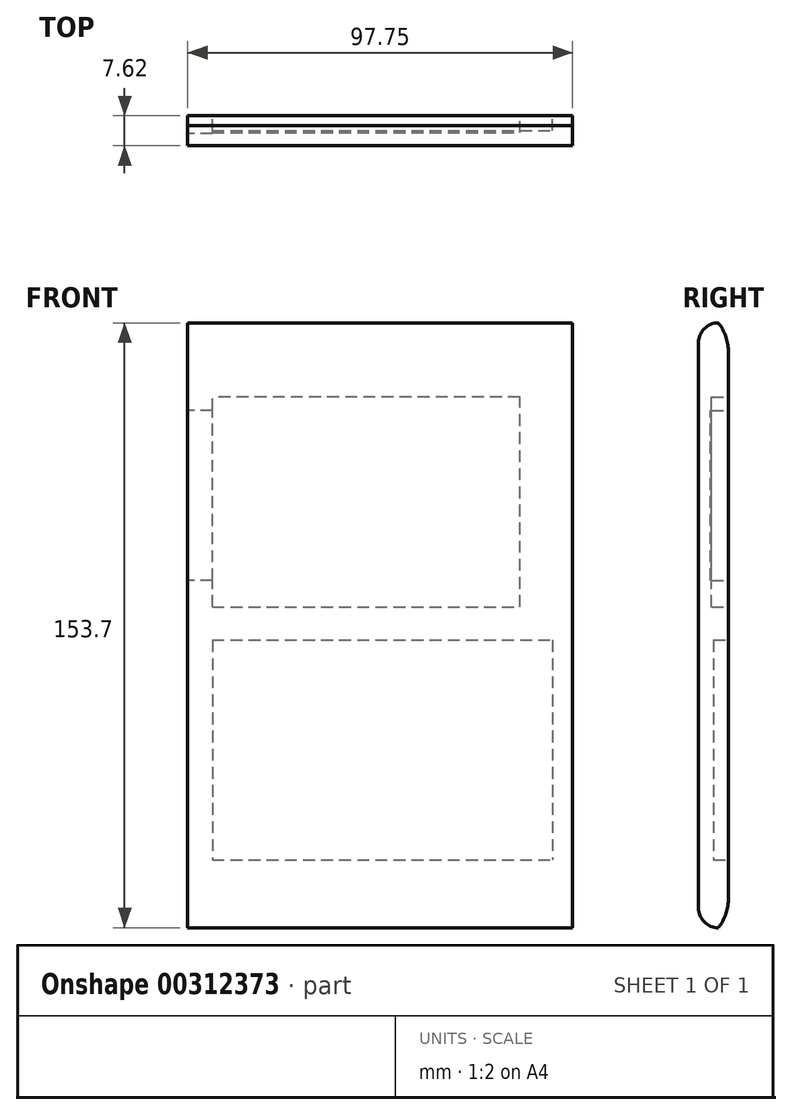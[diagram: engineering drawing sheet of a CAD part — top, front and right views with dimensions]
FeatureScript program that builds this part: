
annotation { "Feature Type Name" : "Feature", "Feature Type Description" : "" }
export const myFeature = defineFeature(function(context is Context, id is Id, definition is map)
    precondition{}
    {
        {
            var Q0;
            Q0=qCreatedBy(makeId("Front.planeOp"),FACE);
            var sketch = newSketch(context, id + "F0", { "sketchPlane" : qUnion([Q0])});
            skLineSegment(sketch, "E0", {"start": v(0, 0) * mm, "end": v(0, 53.34) * mm});
            skLineSegment(sketch, "E1", {"start": v(0, 53.34) * mm, "end": v(64.52, 53.34) * mm});
            skPoint(sketch, "E2", {"position": v(64.52, 53.34) * mm});
            skPoint(sketch, "E3", {"position": v(66.74, 51.82) * mm});
            skPoint(sketch, "E4", {"position": v(66.74, 40.39) * mm});
            skPoint(sketch, "E5", {"position": v(70.53, 37.85) * mm});
            skPoint(sketch, "E6", {"position": v(70.53, 5.08) * mm});
            skPoint(sketch, "E7", {"position": v(66.59, 2.54) * mm});
            skLineSegment(sketch, "E8", {"start": v(0, 0) * mm, "end": v(66.59, 0) * mm});
            skPoint(sketch, "E9.center.orphan", {"position": v(15.24, 50.8) * mm});
            skPoint(sketch, "E10.center.orphan", {"position": v(66.04, 35.56) * mm});
            skPoint(sketch, "E11.center.orphan", {"position": v(66.04, 7.62) * mm});
            skPoint(sketch, "E12.center.orphan", {"position": v(13.97, 2.54) * mm});
            skLineSegment(sketch, "E13", {"start": v(66.59, 0) * mm, "end": v(70.53, 0) * mm});
            skLineSegment(sketch, "E14", {"start": v(64.52, 53.34) * mm, "end": v(70.53, 53.34) * mm});
            skLineSegment(sketch, "E15", {"start": v(70.53, 0) * mm, "end": v(78.15, 0) * mm});
            skLineSegment(sketch, "E16", {"start": v(78.15, 0) * mm, "end": v(78.15, 53.34) * mm});
            skLineSegment(sketch, "E17", {"start": v(78.15, 53.34) * mm, "end": v(70.53, 53.34) * mm});
            skSolve(sketch);
        }
        {
            var Q0;
            Q0=qCreatedBy(makeId("Front.planeOp"),FACE);
            var sketch = newSketch(context, id + "F1", { "sketchPlane" : qUnion([Q0])});
            skLineSegment(sketch, "E18.bottom", {"start": v(0, -8.44) * mm, "end": v(86.36, -8.44) * mm});
            skLineSegment(sketch, "E18.top", {"start": v(0, -64.32) * mm, "end": v(86.36, -64.32) * mm});
            skLineSegment(sketch, "E18.left", {"start": v(0, -8.44) * mm, "end": v(0, -64.32) * mm});
            skLineSegment(sketch, "E18.right", {"start": v(86.36, -8.44) * mm, "end": v(86.36, -64.32) * mm});
            skSolve(sketch);
        }
        {
            var Q0;
            Q0=qCreatedBy(makeId("Front.planeOp"),FACE);
            var sketch = newSketch(context, id + "F2", { "sketchPlane" : qUnion([Q0])});
            skLineSegment(sketch, "E19.left", {"start": v(-6.27, 59.48) * mm, "end": v(-6.27, -68.82) * mm});
            skLineSegment(sketch, "E19.right", {"start": v(91.48, 59.48) * mm, "end": v(91.48, -68.82) * mm});
            skLineSegment(sketch, "E20", {"start": v(-6.27, 59.48) * mm, "end": v(-6.27, 72.18) * mm});
            skLineSegment(sketch, "E21", {"start": v(-6.27, 72.18) * mm, "end": v(91.48, 72.18) * mm});
            skLineSegment(sketch, "E22", {"start": v(91.48, 72.18) * mm, "end": v(91.48, 59.48) * mm});
            skLineSegment(sketch, "E23", {"start": v(-6.27, -68.82) * mm, "end": v(-6.27, -81.52) * mm});
            skLineSegment(sketch, "E24", {"start": v(-6.27, -81.52) * mm, "end": v(91.48, -81.52) * mm});
            skLineSegment(sketch, "E25", {"start": v(91.48, -81.52) * mm, "end": v(91.48, -68.82) * mm});
            skSolve(sketch);
        }
        {
            var Q0;
            Q0 = qSketchRegion(id + "F2", true);
            extrude(context, id + "F3", {"entities" : qUnion([Q0]), "depth" : 7.62 * mm});
        }
        {
            var Q0;
            Q0 = qSketchRegion(id + "F0", true);
            extrude(context, id + "F4", {"entities" : qUnion([Q0]), "operationType" : NewBodyOperationType.REMOVE, "depth" : 4.32 * mm});
        }
        {
            var Q0;
            Q0 = qSketchRegion(id + "F1", true);
            extrude(context, id + "F5", {"entities" : qUnion([Q0]), "operationType" : NewBodyOperationType.REMOVE, "depth" : 3.8 * mm});
        }
        {
            var Q0;
            Q0=makeQuery(id+"F3.opExtrude","CAP_FACE",FACE,{"disambiguationData":[OSD([sQuery(id+"F2.wireOp",EDGE,"E19.left"),sQuery(id+"F2.wireOp",EDGE,"E19.right"),sQuery(id+"F2.wireOp",EDGE,"E20"),sQuery(id+"F2.wireOp",EDGE,"E21"),sQuery(id+"F2.wireOp",EDGE,"E22"),sQuery(id+"F2.wireOp",EDGE,"E23"),sQuery(id+"F2.wireOp",EDGE,"E24"),sQuery(id+"F2.wireOp",EDGE,"E25")])],"isStart":true});
            var sketch = newSketch(context, id + "F6", { "sketchPlane" : qUnion([Q0])});
            skLineSegment(sketch, "E26.bottom", {"start": v(0, 6.77) * mm, "end": v(6.27, 6.77) * mm});
            skLineSegment(sketch, "E26.top", {"start": v(0, 49.92) * mm, "end": v(6.27, 49.92) * mm});
            skLineSegment(sketch, "E26.left", {"start": v(0, 6.77) * mm, "end": v(0, 49.92) * mm});
            skLineSegment(sketch, "E26.right", {"start": v(6.27, 6.77) * mm, "end": v(6.27, 49.92) * mm});
            skSolve(sketch);
        }
        {
            var Q0;
            Q0 = qSketchRegion(id + "F6", true);
            extrude(context, id + "F7", {"entities" : qUnion([Q0]), "operationType" : NewBodyOperationType.REMOVE, "oppositeDirection" : true, "depth" : 4.57 * mm});
        }
        {
            var Q0;
            Q0=makeQuery(id+"F3.opExtrude","CAP_EDGE",EDGE,{"disambiguationData":[OSD([sQuery(id+"F2.wireOp",EDGE,"E24")])],"isStart":false});
            fillet(context, id + "F8", {"entities" : qUnion([Q0]), "radius" : 5.08 * mm, "tangentPropagation" : true, "allowEdgeOverflow" : false});
        }
        {
            var Q0;
            Q0=makeQuery(id+"F3.opExtrude","CAP_EDGE",EDGE,{"disambiguationData":[OSD([sQuery(id+"F2.wireOp",EDGE,"E24")])],"isStart":true});
            fillet(context, id + "F9", {"entities" : qUnion([Q0]), "radius" : 12.7 * mm, "tangentPropagation" : true, "allowEdgeOverflow" : false});
        }
        {
            var Q0;
            Q0=makeQuery(id+"F3.opExtrude","CAP_EDGE",EDGE,{"disambiguationData":[OSD([sQuery(id+"F2.wireOp",EDGE,"E21")])],"isStart":false});
            fillet(context, id + "F10", {"entities" : qUnion([Q0]), "radius" : 5.08 * mm, "tangentPropagation" : true, "allowEdgeOverflow" : false});
        }
        {
            var Q0;
            Q0=makeQuery(id+"F3.opExtrude","CAP_EDGE",EDGE,{"disambiguationData":[OSD([sQuery(id+"F2.wireOp",EDGE,"E21")])],"isStart":true});
            fillet(context, id + "F11", {"entities" : qUnion([Q0]), "radius" : 12.7 * mm, "tangentPropagation" : true, "allowEdgeOverflow" : false});
        }
    });
